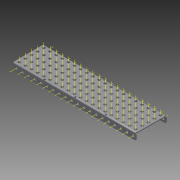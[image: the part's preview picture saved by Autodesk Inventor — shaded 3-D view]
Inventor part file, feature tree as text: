
AUTODESK INVENTOR PART (.ipt)
format: ipt  version: 2015 (Build 190159000, 159)  size: 2,628,608 bytes
history: native  units: in
note: dims shown in document units (in); Inventor stores cm internally (conversion verified against a paired STEP export)
features: other x146, pattern_linear x2, sheet_metal_op x1, extrude x1, imported_body x1, sketch x1
ambient origin geometry x8: Origin, YZ Plane, XZ Plane, XY Plane, X Axis, Y Axis, Z Axis, Center Point
bodies: Body1 (feature_tree)
feature tree (152):
  sheet_metal_op  "Fold1"
  other  "C-Channel"
  extrude  "length cut"  Depth=0.5in
  other  "top axis"
  other  "front axis"
  other  "back axis"
  pattern_linear  "top axes"  Spacing1=0.5in  [1 undecoded]
  pattern_linear  "horiz axes"  Spacing1=0.0in  [1 undecoded]
  other  "right plane"
  imported_body  "Base1"
  sketch  "Sketch1"  dims[d1=0.0in d4=0.5in d5=1.9685in d7=0.5in d10=0.5in d11=0.0in d12=0.0in d13=0.0in d14=-10.0in d15=0.0in d16=0.0in]
  other  "Work Point1"
  other  "Work Axis6"
  other  "Work Axis11"
  other  "Work Axis16"
  other  "Work Axis21"
  other  "Work Point2"
  other  "Work Point3"
  other  "Work Axis36"
  other  "Work Axis37"
  other  "Work Axis38"
  other  "Work Axis39"
  other  "Work Axis40"
  other  "Work Axis41"
  other  "Work Axis60"
  other  "Work Axis61"
  other  "Work Axis62"
  other  "Work Axis63"
  other  "Work Axis64"
  other  "Work Axis65"
  other  "Work Axis84"
  other  "Work Axis85"
  other  "Work Axis86"
  other  "Work Axis87"
  other  "Work Axis88"
  other  "Work Axis89"
  other  "Work Axis108"
  other  "Work Axis109"
  other  "Work Axis110"
  other  "Work Axis111"
  other  "Work Axis112"
  other  "Work Axis113"
  other  "Work Axis132"
  other  "Work Axis133"
  other  "Work Axis134"
  other  "Work Axis135"
  other  "Work Axis136"
  other  "Work Axis137"
  other  "Work Axis156"
  other  "Work Axis157"
  other  "Work Axis158"
  other  "Work Axis159"
  other  "Work Axis160"
  other  "Work Axis161"
  other  "Work Axis180"
  other  "Work Axis181"
  other  "Work Axis182"
  other  "Work Axis183"
  other  "Work Axis184"
  other  "Work Axis185"
  other  "Work Axis204"
  other  "Work Axis205"
  other  "Work Axis206"
  other  "Work Axis207"
  other  "Work Axis208"
  other  "Work Axis209"
  other  "Work Axis210"
  other  "Work Axis211"
  other  "Work Axis212"
  other  "Work Axis213"
  other  "Work Axis214"
  other  "Work Axis215"
  other  "Work Axis216"
  other  "Work Axis232"
  other  "Work Axis233"
  other  "Work Axis234"
  other  "Work Axis235"
  other  "Work Axis236"
  other  "Work Axis237"
  other  "Work Axis238"
  other  "Work Axis239"
  other  "Work Axis240"
  other  "Work Axis241"
  other  "Work Axis242"
  other  "Work Axis243"
  other  "Work Axis244"
  other  "Work Axis260"
  other  "Work Axis261"
  other  "Work Axis262"
  other  "Work Axis263"
  other  "Work Axis264"
  other  "Work Axis265"
  other  "Work Axis266"
  other  "Work Axis267"
  other  "Work Axis268"
  other  "Work Axis269"
  other  "Work Axis270"
  other  "Work Axis271"
  other  "Work Axis272"
  other  "Work Axis288"
  other  "Work Axis289"
  other  "Work Axis290"
  other  "Work Axis291"
  other  "Work Axis292"
  other  "Work Axis293"
  other  "Work Axis294"
  other  "Work Axis295"
  other  "Work Axis296"
  other  "Work Axis297"
  other  "Work Axis298"
  other  "Work Axis299"
  other  "Work Axis300"
  other  "Work Axis316"
  other  "Work Axis317"
  other  "Work Axis318"
  other  "Work Axis319"
  other  "Work Axis320"
  other  "Work Axis321"
  other  "Work Axis322"
  other  "Work Axis323"
  other  "Work Axis324"
  other  "Work Axis325"
  other  "Work Axis326"
  other  "Work Axis327"
  other  "Work Axis328"
  other  "Work Axis344"
  other  "Work Axis345"
  other  "Work Axis346"
  other  "Work Axis347"
  other  "Work Axis348"
  other  "Work Axis349"
  other  "Work Axis350"
  other  "Work Axis351"
  other  "Work Axis352"
  other  "Work Axis353"
  other  "Work Axis354"
  other  "Work Axis355"
  other  "Work Axis356"
  other  "Work Axis372"
  other  "Work Axis373"
  other  "Work Axis374"
  other  "Work Axis375"
  other  "Work Axis376"
  other  "Work Axis377"
  other  "Work Axis378"
  other  "Work Axis379"
  other  "Work Axis380"
  other  "Work Axis381"
  other  "Work Axis382"
  other  "Work Axis383"
  other  "Work Axis384"
  other  "left plane"
note: 2 required parameter values undecoded (feature->parameter linkage not recoverable at this tier; creation-order binding heuristic only, values carry confidence <= 0.55)
